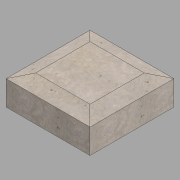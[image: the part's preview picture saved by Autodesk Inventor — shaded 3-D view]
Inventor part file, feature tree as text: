
AUTODESK INVENTOR PART (.ipt)
format: ipt  version: 2022.1 (Build 261234020, 234B)  size: 122,880 bytes
history: native  units: in
note: dims shown in document units (in); Inventor stores cm internally (conversion verified against a paired STEP export)
features: sketch x3, extrude x1, sweep x1
ambient origin geometry x8: Origin, YZ Plane, XZ Plane, XY Plane, X Axis, Y Axis, Z Axis, Center Point
bodies: Solid1 (feature_tree)
feature tree (5):
  extrude  "Extrusion1"  Depth=34.0in
  sweep  "Sweep1"
  sketch  "Sketch1"  dims[d0=34.0in d1=34.0in]
  sketch  "Sketch2"  dims[d2=12.0in d3=0.0in d4=6.0in d5=2.0in d6=0.0in d7=0.0in]
  sketch  "3D Sketch1"
